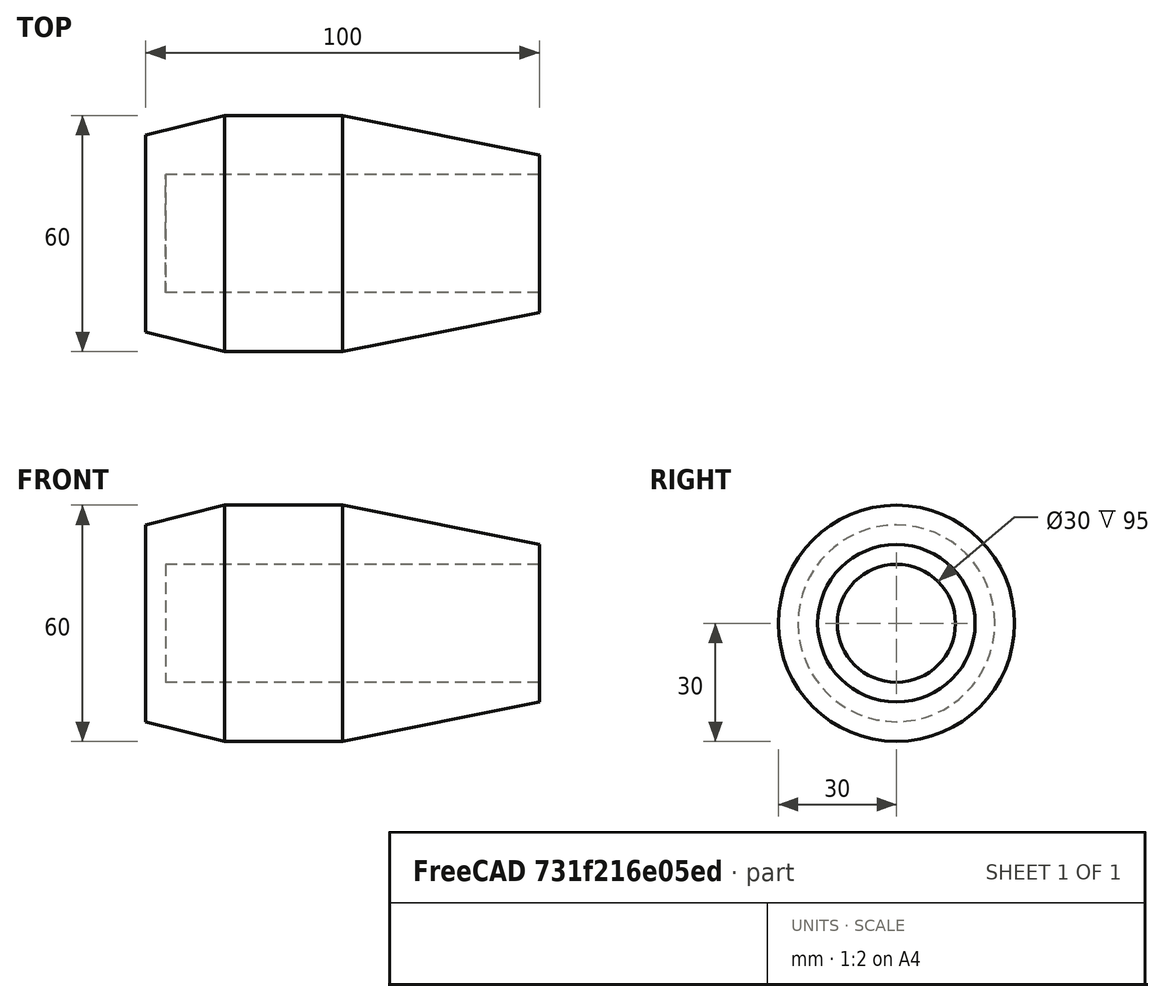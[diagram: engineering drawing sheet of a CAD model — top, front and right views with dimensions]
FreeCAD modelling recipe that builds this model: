
FCSTD DOCUMENT  (FreeCAD 0.18.4R)
Label: cannon-body
License: All rights reserved
LicenseURL: http://en.wikipedia.org/wiki/All_rights_reserved
objects: Sketcher::SketchObject×1, PartDesign::Revolution×1, PartDesign::Body×1
note: 4 computed .brp shape members not serialized (recipe doc carries the construction recipe); baked Part::Feature solids carry a one-line shape summary decoded from their .brp

FEATURE [Sketcher::SketchObject] Sketch
  MapMode = 5
  Placement = pos=(0,0,0) rot=(1,0,0;1.5708rad)
  Support = -> [XZ_Plane]
  sketch-geometry (8):
    g0: LineSegment StartX=-35 StartY=0 StartZ=0 EndX=-35 EndY=25 EndZ=0
    g1: LineSegment StartX=-35 StartY=25 StartZ=0 EndX=-15 EndY=30 EndZ=0
    g2: LineSegment StartX=-15 StartY=30 StartZ=0 EndX=15 EndY=30 EndZ=0
    g3: LineSegment StartX=15 StartY=30 StartZ=0 EndX=65 EndY=20 EndZ=0
    g4: LineSegment StartX=65 StartY=20 StartZ=0 EndX=65 EndY=15 EndZ=0
    g5: LineSegment StartX=65 StartY=15 StartZ=0 EndX=-30 EndY=15 EndZ=0
    g6: LineSegment StartX=-30 StartY=15 StartZ=0 EndX=-30 EndY=0 EndZ=0
    g7: LineSegment StartX=-30 StartY=0 StartZ=0 EndX=-35 EndY=0 EndZ=0
  constraints (22):
    c: Vertical(g0)
    c: Coincident(g0,g1)
    c: Coincident(g1,g2)
    c: Horizontal(g2)
    c: Coincident(g2,g3)
    c: Coincident(g3,g4)
    c: Vertical(g4)
    c: Coincident(g4,g5)
    c: Horizontal(g5)
    c: Coincident(g5,g6)
    c: Vertical(g6)
    c: Coincident(g6,g7)
    c: Coincident(g7,g0)
    c: Horizontal(g7)
    c: DistanceX(g2,g2) = 30
    c: DistanceX(g0,g1) = 20
    c: DistanceX(g0,g3) = 100
    c: DistanceX(g1,g-1) = 15
    c: DistanceX(g7,g7) = 5
    c: DistanceY(g4,g4) = 5
    c: DistanceY(g0,g1) = 30
    c: DistanceY(g6,g6) = 15
FEATURE [PartDesign::Revolution] Revolution
  Angle = 360
  Axis = (1,0,0)
  Base = (0,0,0)
  Placement = pos=(0,0,0) rot=(1,0,0;1.5708rad)
  Profile = -> Sketch
  ReferenceAxis = -> X_Axis
  Reversed = true
FEATURE [PartDesign::Body] Body
  Group = -> [Sketch,Revolution]
  Origin = -> Origin
  Tip = -> Revolution
